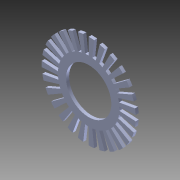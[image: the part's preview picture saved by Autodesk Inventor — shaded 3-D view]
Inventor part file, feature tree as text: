
AUTODESK INVENTOR PART (.ipt)
format: ipt  version: 2011 (Build 150239000, 239)  size: 583,168 bytes
history: native  units: in
note: dims shown in document units (in); Inventor stores cm internally (conversion verified against a paired STEP export)
features: extrude x5, sketch x5, imported_body x1, other x1
ambient origin geometry x8: Origin, YZ Plane, XZ Plane, XY Plane, X Axis, Y Axis, Z Axis, Center Point
feature tree (12):
  imported_body  "Base112"
  extrude  "Extrusion1"  Depth=0.65in
  extrude  "Extrusion2"  Depth=10.6299in TaperAngle=360.0deg
  extrude  "Extrusion3"  Depth=10.6299in TaperAngle=360.0deg
  extrude  "Extrusion4"  Depth=0.042in TaperAngle=0.0deg
  extrude  "Extrusion5"  [1 undecoded]
  other  "27971 - Motor Mount and Wheel Kit (v1.0)_111"
  sketch  "Sketch1"  dims[d0=1.0in d1=0.0in d2=0.65in]
  sketch  "Sketch2"  dims[d3=0.0458in d4=10.6299in d6=360.0deg]
  sketch  "Sketch3"  dims[d8=0.042in d9=0.0in d10=10.6299in d12=360.0deg]
  sketch  "Sketch4"  dims[d14=0.042in d15=0.0in d16=0.042in d17=0.0in]
  sketch  "Sketch5"  dims[d18=1.0in d19=0.0in]
note: 1 required parameter value undecoded (feature->parameter linkage not recoverable at this tier; creation-order binding heuristic only, values carry confidence <= 0.55)
